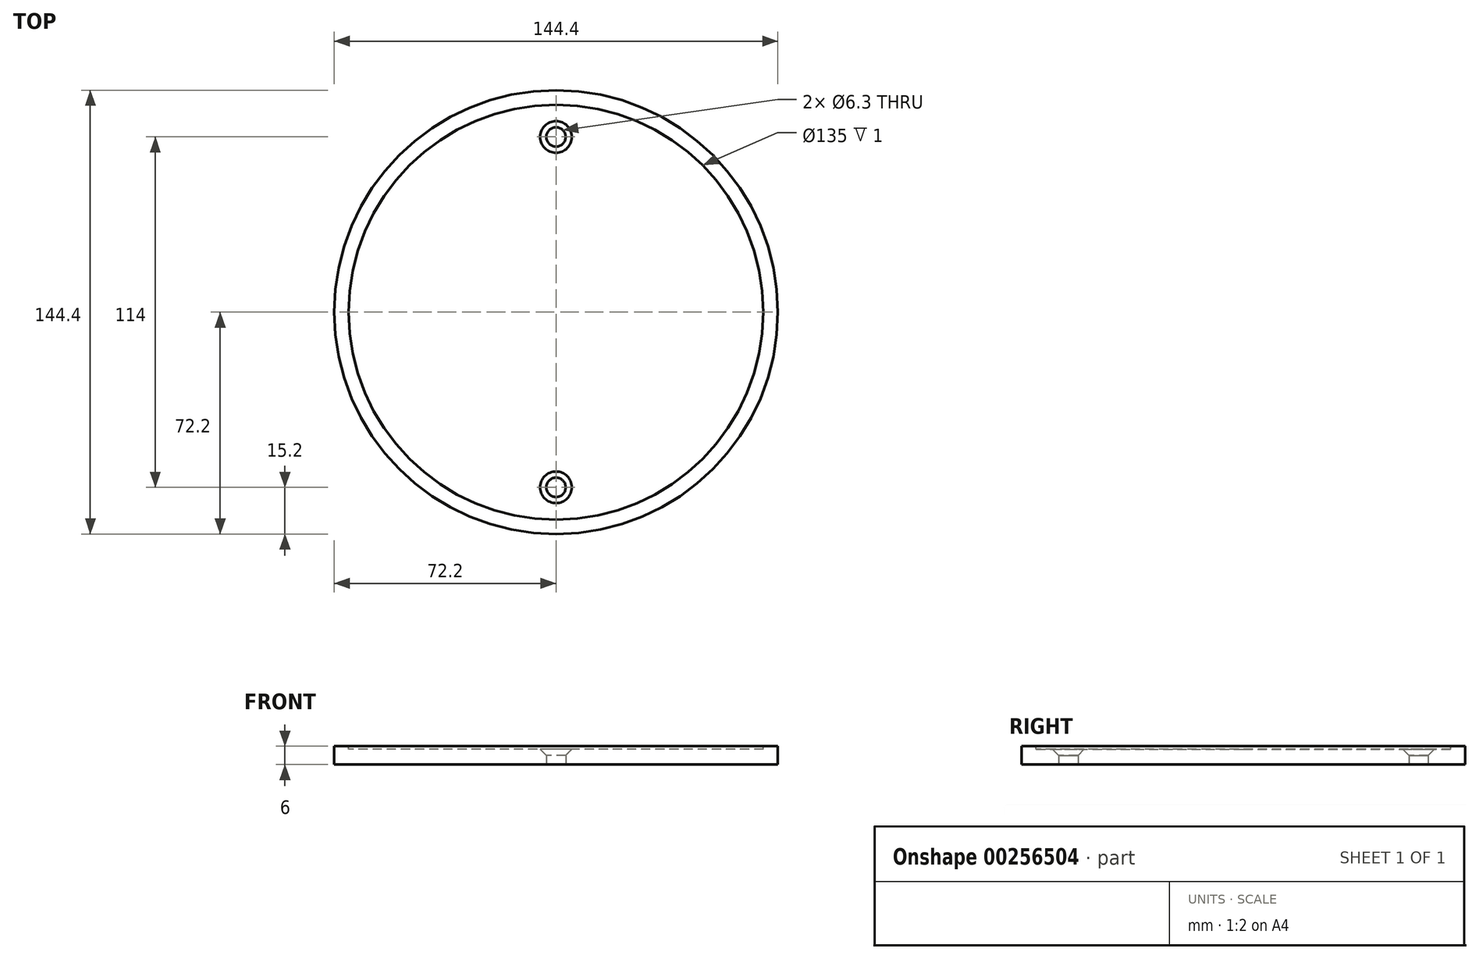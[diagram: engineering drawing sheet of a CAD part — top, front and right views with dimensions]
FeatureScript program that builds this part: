
annotation { "Feature Type Name" : "Feature", "Feature Type Description" : "" }
export const myFeature = defineFeature(function(context is Context, id is Id, definition is map)
    precondition{}
    {
        {
            var Q0;
            Q0=qCreatedBy(makeId("Top.planeOp"),FACE);
            var sketch = newSketch(context, id + "F0", { "sketchPlane" : qUnion([Q0])});
            skCircle(sketch, "E0", {"center": v(0, 0) * mm, "radius": 24.07 * mm});
            skCircle(sketch, "E1", {"center": v(0, 19) * mm, "radius": 1.05 * mm});
            skCircle(sketch, "E2", {"center": v(0, -19) * mm, "radius": 1.05 * mm});
            skSolve(sketch);
        }
        {
            var Q0;
            Q0=makeQuery(id+"F0.imprint","IMPRINT",FACE,{"disambiguationData":[TD([[makeQuery(id+"F0.imprint","IMPRINT",EDGE,{"derivedFrom":sQuery(id+"F0.wireOp",EDGE,"E0")}),1.0]])]});
            extrude(context, id + "F1", {"entities" : qUnion([Q0]), "depth" : 2 * mm});
        }
        {
            var Q0;
            Q0=makeQuery(id+"F1.opExtrude","CAP_EDGE",EDGE,{"disambiguationData":[OSD([sQuery(id+"F0.wireOp",EDGE,"E1")])],"isStart":false});
            var Q1;
            Q1=makeQuery(id+"F1.opExtrude","CAP_EDGE",EDGE,{"disambiguationData":[OSD([sQuery(id+"F0.wireOp",EDGE,"E2")])],"isStart":false});
            chamfer(context, id + "F2", {"entities" : qUnion([Q0, Q1]), "width" : 1 * mm, "tangentPropagation" : true});
        }
        {
            var Q0;
            Q0=makeQuery(id+"F1.opExtrude","SWEPT_BODY",BODY,{"disambiguationData":[OSD([sQuery(id+"F0.wireOp",EDGE,"E0"),sQuery(id+"F0.wireOp",EDGE,"E1"),sQuery(id+"F0.wireOp",EDGE,"E2")])]});
            var Q1;
            Q1=qCreatedBy(makeId("Origin.pointOp"),VERTEX);
            transform(context, id + "F3", {"entities" : qUnion([Q0]), "transformType" : TransformType.SCALE_UNIFORMLY, "scale" : 3, "makeCopy" : false, "scalePoint" : qUnion([Q1])});
        }
        {
            var Q0;
            Q0=makeQuery(id+"F1.opExtrude","CAP_FACE",FACE,{"disambiguationData":[OSD([sQuery(id+"F0.wireOp",EDGE,"E0"),sQuery(id+"F0.wireOp",EDGE,"E1"),sQuery(id+"F0.wireOp",EDGE,"E2")])],"isStart":false});
            var sketch = newSketch(context, id + "F4", { "sketchPlane" : qUnion([Q0])});
            skCircle(sketch, "E3", {"center": v(0, 0) * mm, "radius": 67.5 * mm});
            skSolve(sketch);
        }
        {
            var Q0;
            Q0 = qSketchRegion(id + "F4", true);
            extrude(context, id + "F5", {"entities" : qUnion([Q0]), "operationType" : NewBodyOperationType.REMOVE, "oppositeDirection" : true, "depth" : 1 * mm});
        }
    });
